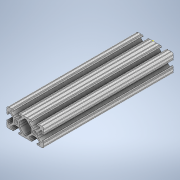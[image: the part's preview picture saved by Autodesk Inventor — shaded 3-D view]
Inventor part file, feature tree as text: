
AUTODESK INVENTOR PART (.ipt)
format: ipt  version: 2020 (Build 240168000, 168)  size: 333,824 bytes
history: native  units: in
note: dims shown in document units (in); Inventor stores cm internally (conversion verified against a paired STEP export)
features: sketch x4, extrude x1
ambient origin geometry x8: Origin, YZ Plane, XZ Plane, XY Plane, X Axis, Y Axis, Z Axis, Center Point
bodies: Solid1 (feature_tree)
feature tree (5):
  extrude  "Extrusion1"  [1 undecoded]
  sketch  "Sketch2"
  sketch  "Sketch3"
  sketch  "Sketch4"
  sketch  "Sketch1"  dims[d0=7.0in d1=0.0in]
note: 1 required parameter value undecoded (feature->parameter linkage not recoverable at this tier; creation-order binding heuristic only, values carry confidence <= 0.55)
